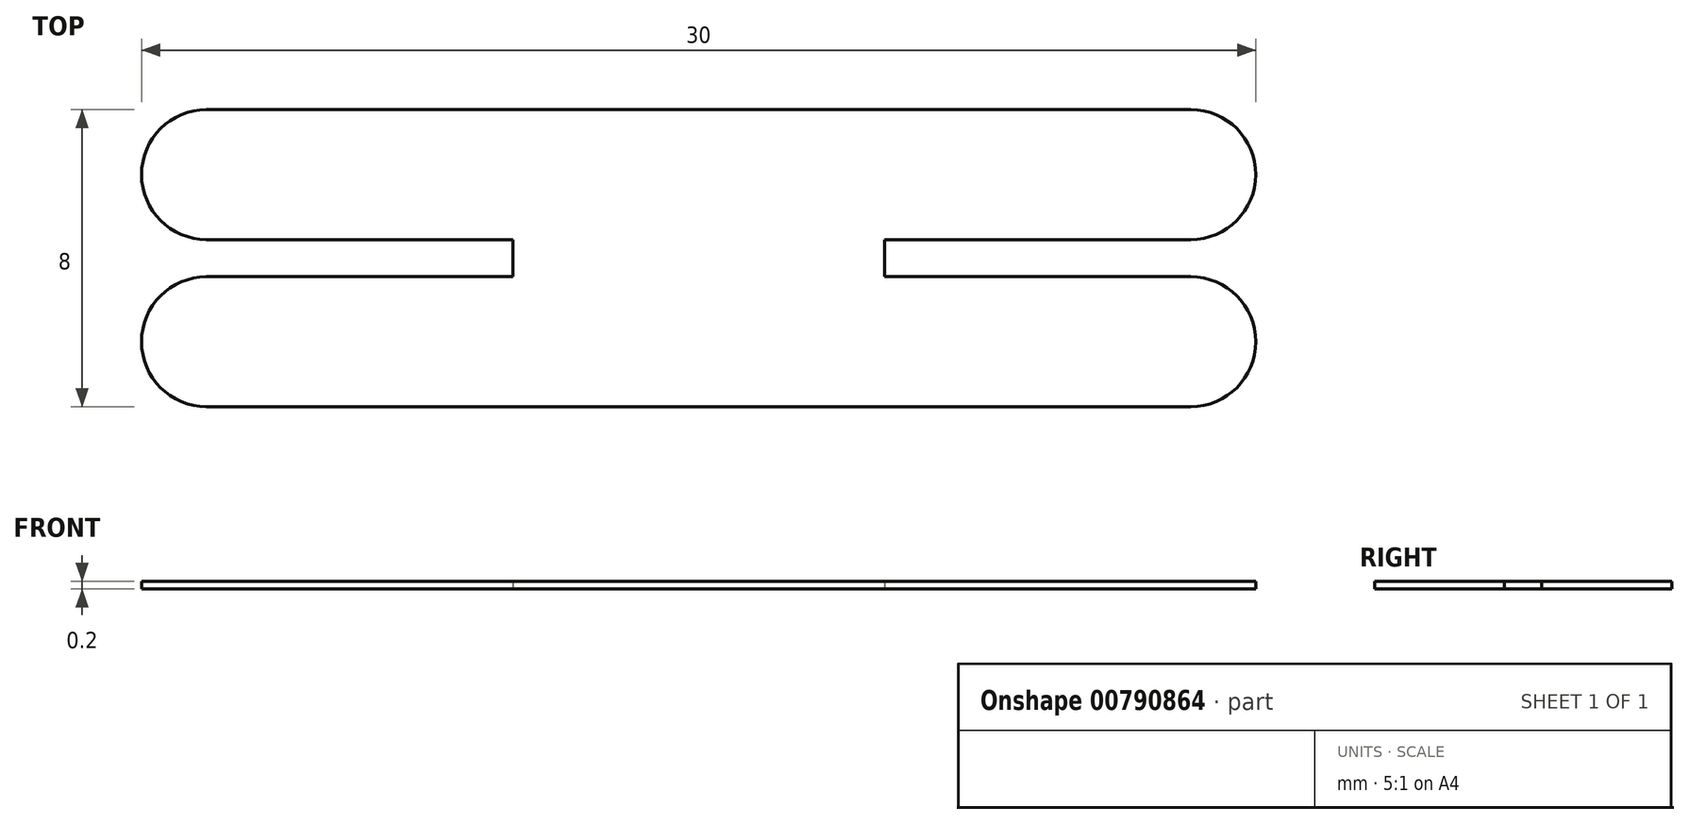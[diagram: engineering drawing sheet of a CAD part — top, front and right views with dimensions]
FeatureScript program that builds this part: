
annotation { "Feature Type Name" : "Feature", "Feature Type Description" : "" }
export const myFeature = defineFeature(function(context is Context, id is Id, definition is map)
    precondition{}
    {
        {
            var Q0;
            Q0=qCreatedBy(makeId("Top.planeOp"),FACE);
            var sketch = newSketch(context, id + "F0", { "sketchPlane" : qUnion([Q0])});
            skLineSegment(sketch, "E0.bottom", {"start": v(13.25, 4) * mm, "end": v(-13.25, 4) * mm});
            skLineSegment(sketch, "E0.top", {"start": v(13.25, -4) * mm, "end": v(-13.25, -4) * mm});
            skLineSegment(sketch, "E0.left", {"start": v(15, 2.25) * mm, "end": v(15, 2.25) * mm});
            skLineSegment(sketch, "E0.right", {"start": v(-15, 2.25) * mm, "end": v(-15, 2.25) * mm});
            skPoint(sketch, "E0.middle", {"position": v(0, 0) * mm});
            skLineSegment(sketch, "E1.bottom", {"start": v(-5, 0.5) * mm, "end": v(-13.25, 0.5) * mm});
            skLineSegment(sketch, "E1.top", {"start": v(-5, -0.5) * mm, "end": v(-13.25, -0.5) * mm});
            skLineSegment(sketch, "E1.left", {"start": v(-5, 0.5) * mm, "end": v(-5, -0.5) * mm});
            skLineSegment(sketch, "E1.right", {"start": v(-25, 0.5) * mm, "end": v(-25, -0.5) * mm});
            skPoint(sketch, "E1.middle", {"position": v(-15, 0) * mm});
            skLineSegment(sketch, "E2.bottom", {"start": v(13.25, -0.5) * mm, "end": v(5, -0.5) * mm});
            skLineSegment(sketch, "E2.top", {"start": v(13.25, 0.5) * mm, "end": v(5, 0.5) * mm});
            skLineSegment(sketch, "E2.left", {"start": v(25, -0.5) * mm, "end": v(25, 0.5) * mm});
            skLineSegment(sketch, "E2.right", {"start": v(5, -0.5) * mm, "end": v(5, 0.5) * mm});
            skPoint(sketch, "E2.middle", {"position": v(15, 0) * mm});
            skPoint(sketch, "E3.newPointA", {"position": v(-15, -4) * mm});
            skPoint(sketch, "E3.newPointB", {"position": v(-25, 0.5) * mm});
            skArc(sketch, "E3.filletArc", {"start": v(-15, 2.25) * mm, "mid": v(-14.49, 1.01) * mm, "end": v(-13.25, 0.5) * mm});
            skPoint(sketch, "E4.visualSharp", {"position": v(-15, 4) * mm});
            skArc(sketch, "E4.filletArc", {"start": v(-13.25, 4) * mm, "mid": v(-14.49, 3.49) * mm, "end": v(-15, 2.25) * mm});
            skLineSegment(sketch, "E5", {"start": v(-15, -2.25) * mm, "end": v(-15, -2.25) * mm});
            skArc(sketch, "E6.filletArc", {"start": v(-15, -2.25) * mm, "mid": v(-14.49, -3.49) * mm, "end": v(-13.25, -4) * mm});
            skPoint(sketch, "E7.newPointA", {"position": v(-15, -0.5) * mm});
            skPoint(sketch, "E7.newPointB", {"position": v(-25, -0.5) * mm});
            skArc(sketch, "E7.filletArc", {"start": v(-13.25, -0.5) * mm, "mid": v(-14.49, -1.01) * mm, "end": v(-15, -2.25) * mm});
            skPoint(sketch, "E8.visualSharp", {"position": v(15, -4) * mm});
            skArc(sketch, "E8.filletArc", {"start": v(13.25, -4) * mm, "mid": v(14.49, -3.49) * mm, "end": v(15, -2.25) * mm});
            skPoint(sketch, "E9.visualSharp", {"position": v(15, 4) * mm});
            skArc(sketch, "E9.filletArc", {"start": v(15, 2.25) * mm, "mid": v(14.49, 3.49) * mm, "end": v(13.25, 4) * mm});
            skPoint(sketch, "E10.newPointB", {"position": v(25, 0.5) * mm});
            skArc(sketch, "E10.filletArc", {"start": v(13.25, 0.5) * mm, "mid": v(14.49, 1.01) * mm, "end": v(15, 2.25) * mm});
            skLineSegment(sketch, "E11", {"start": v(15, -2.25) * mm, "end": v(15, -2.25) * mm});
            skPoint(sketch, "E12.newPointA", {"position": v(25, -0.5) * mm});
            skPoint(sketch, "E12.newPointB", {"position": v(15, -0.5) * mm});
            skArc(sketch, "E12.filletArc", {"start": v(15, -2.25) * mm, "mid": v(14.49, -1.01) * mm, "end": v(13.25, -0.5) * mm});
            skSolve(sketch);
        }
        {
            var Q0;
            Q0=makeQuery(id+"F0.imprint","IMPRINT",FACE,{"disambiguationData":[TD([[makeQuery(id+"F0.imprint","IMPRINT",EDGE,{"derivedFrom":sQuery(id+"F0.wireOp",EDGE,"E0.bottom")}),1.0]])]});
            extrude(context, id + "F1", {"entities" : qUnion([Q0]), "depth" : 0.2 * mm, "offsetDistance" : 25 * mm});
        }
    });
